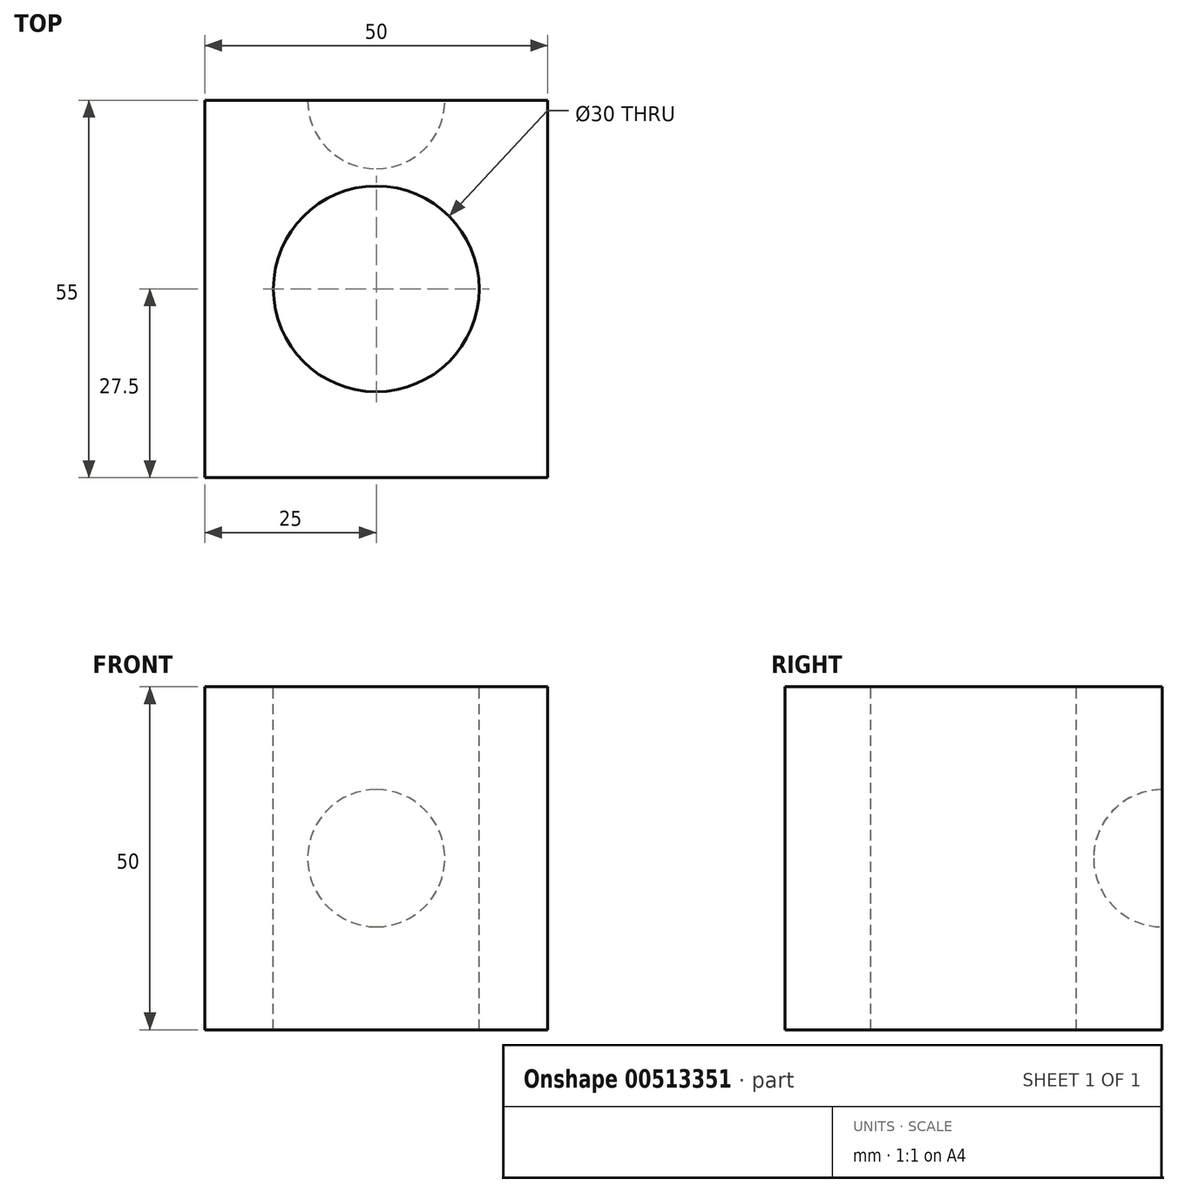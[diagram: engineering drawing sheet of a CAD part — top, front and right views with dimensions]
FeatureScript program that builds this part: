
annotation { "Feature Type Name" : "Feature", "Feature Type Description" : "" }
export const myFeature = defineFeature(function(context is Context, id is Id, definition is map)
    precondition{}
    {
        {
            var Q0;
            Q0=qCreatedBy(makeId("Front.planeOp"),FACE);
            var sketch = newSketch(context, id + "F0", { "sketchPlane" : qUnion([Q0])});
            skLineSegment(sketch, "E0.bottom", {"start": v(25, -25) * mm, "end": v(-25, -25) * mm});
            skLineSegment(sketch, "E0.top", {"start": v(25, 25) * mm, "end": v(-25, 25) * mm});
            skLineSegment(sketch, "E0.left", {"start": v(25, -25) * mm, "end": v(25, 25) * mm});
            skLineSegment(sketch, "E0.right", {"start": v(-25, -25) * mm, "end": v(-25, 25) * mm});
            skPoint(sketch, "E0.middle", {"position": v(0, 0) * mm});
            skSolve(sketch);
        }
        {
            var Q0;
            Q0 = qSketchRegion(id + "F0", true);
            extrude(context, id + "F1", {"entities" : qUnion([Q0]), "depth" : 55 * mm});
        }
        {
            var Q0;
            Q0=makeQuery(id+"F1.opExtrude","SWEPT_FACE",FACE,{"disambiguationData":[OSD([sQuery(id+"F0.wireOp",EDGE,"E0.top")])]});
            var sketch = newSketch(context, id + "F2", { "sketchPlane" : qUnion([Q0])});
            skLineSegment(sketch, "E1", {"start": v(0, 0) * mm, "end": v(0, -55) * mm, "construction": true});
            skLineSegment(sketch, "E2", {"start": v(-25, -27.5) * mm, "end": v(25, -27.5) * mm, "construction": true});
            skCircle(sketch, "E3", {"center": v(0, -27.5) * mm, "radius": 15 * mm});
            skSolve(sketch);
        }
        {
            var Q0;
            Q0 = qSketchRegion(id + "F2", true);
            extrude(context, id + "F3", {"entities" : qUnion([Q0]), "operationType" : NewBodyOperationType.REMOVE, "oppositeDirection" : true, "depth" : 50 * mm});
        }
        {
            var Q0;
            Q0=qCreatedBy(makeId("Right.planeOp"),FACE);
            var sketch = newSketch(context, id + "F4", { "sketchPlane" : qUnion([Q0])});
            skArc(sketch, "E4", {"start": v(0, 10) * mm, "mid": v(-7.07, 7.07) * mm, "end": v(-10, 0) * mm});
            skLineSegment(sketch, "E5", {"start": v(0, 0) * mm, "end": v(0, 10) * mm});
            skLineSegment(sketch, "E6", {"start": v(0, 0) * mm, "end": v(-10, 0) * mm});
            skSolve(sketch);
        }
        {
            var Q0;
            Q0 = qSketchRegion(id + "F4", true);
            var Q1;
            Q1=sQuery(id+"F4.wireOp",EDGE,"E6");
            revolve(context, id + "F5", {"operationType" : NewBodyOperationType.REMOVE, "entities" : qUnion([Q0]), "axis" : qUnion([Q1]), "revolveType" : RevolveType.FULL, "oppositeDirection" : true});
        }
    });
